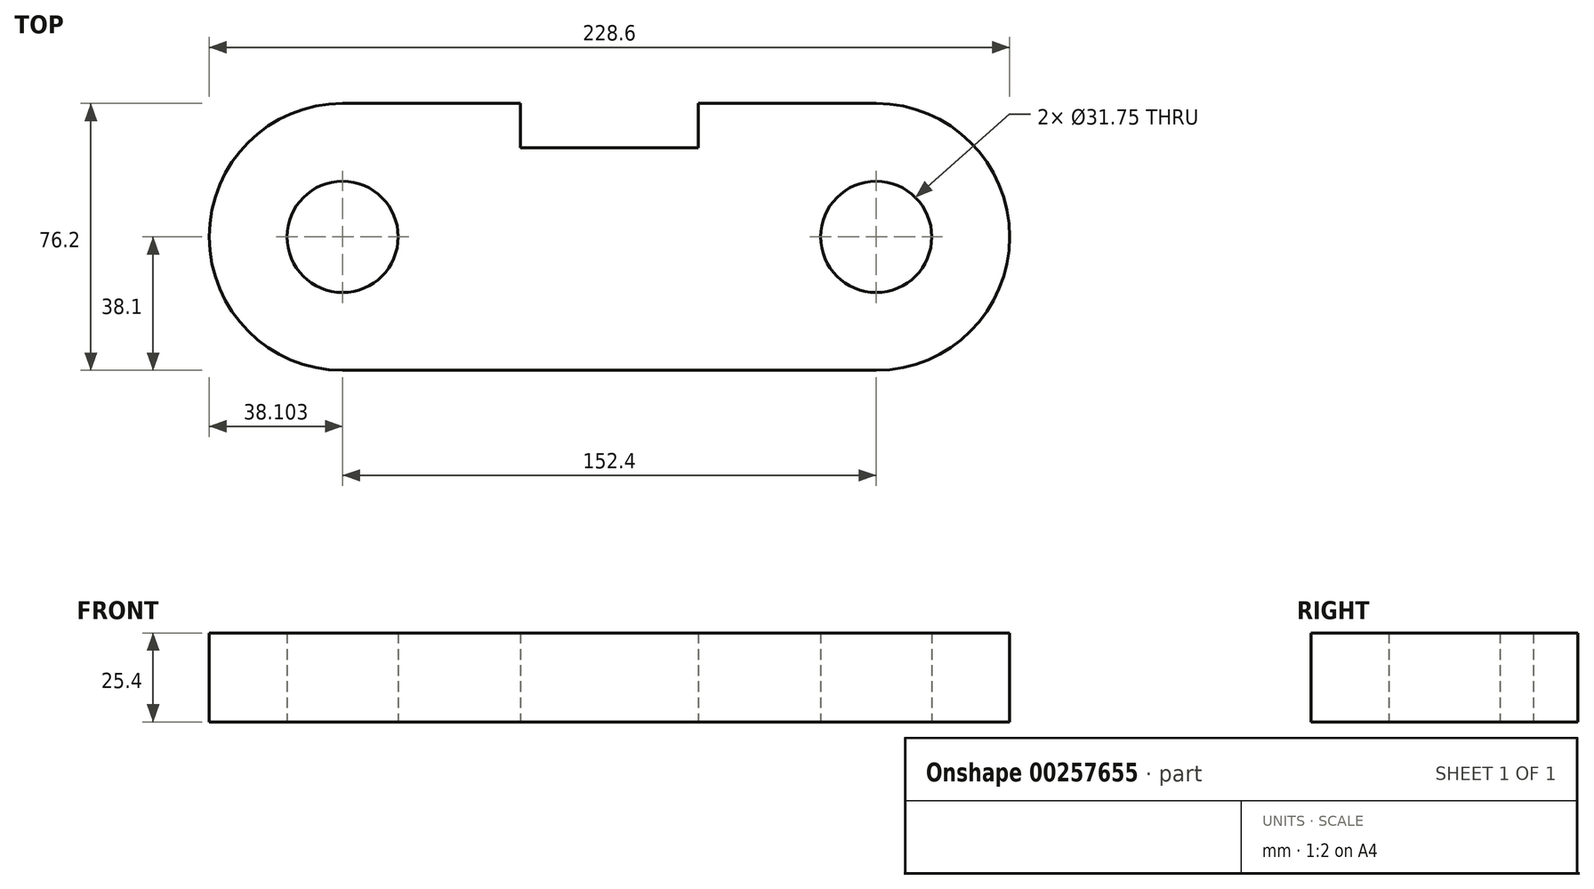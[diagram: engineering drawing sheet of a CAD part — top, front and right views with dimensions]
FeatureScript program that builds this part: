
annotation { "Feature Type Name" : "Feature", "Feature Type Description" : "" }
export const myFeature = defineFeature(function(context is Context, id is Id, definition is map)
    precondition{}
    {
        {
            var Q0;
            Q0=qCreatedBy(makeId("Top.planeOp"),FACE);
            var sketch = newSketch(context, id + "F0", { "sketchPlane" : qUnion([Q0])});
            skCircle(sketch, "E0", {"center": v(-93.82, 0) * mm, "radius": 15.88 * mm});
            skCircle(sketch, "E1", {"center": v(58.58, 0) * mm, "radius": 15.88 * mm});
            skArc(sketch, "E2", {"start": v(58.58, -38.1) * mm, "mid": v(96.68, 0) * mm, "end": v(58.58, 38.1) * mm});
            skArc(sketch, "E3", {"start": v(-93.82, 38.1) * mm, "mid": v(-131.92, 0) * mm, "end": v(-93.82, -38.1) * mm});
            skLineSegment(sketch, "E4", {"start": v(58.58, -38.1) * mm, "end": v(-93.82, -38.1) * mm});
            skLineSegment(sketch, "E5", {"start": v(-93.82, 38.1) * mm, "end": v(-43.02, 38.1) * mm});
            skLineSegment(sketch, "E6", {"start": v(-43.02, 38.1) * mm, "end": v(-43.02, 25.4) * mm});
            skLineSegment(sketch, "E7", {"start": v(-43.02, 25.4) * mm, "end": v(7.78, 25.4) * mm});
            skLineSegment(sketch, "E8", {"start": v(7.78, 25.4) * mm, "end": v(7.78, 38.1) * mm});
            skLineSegment(sketch, "E9", {"start": v(7.78, 38.1) * mm, "end": v(58.58, 38.1) * mm});
            skSolve(sketch);
        }
        {
            var Q0;
            Q0 = qSketchRegion(id + "F0", true);
            extrude(context, id + "F1", {"entities" : qUnion([Q0]), "depth" : 25.4 * mm});
        }
    });
